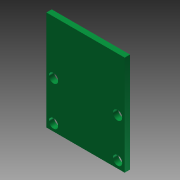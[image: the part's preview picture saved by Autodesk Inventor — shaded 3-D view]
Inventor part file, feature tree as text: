
AUTODESK INVENTOR PART (.ipt)
format: ipt  version: 2014 SP1 (Build 180222100, 222)  size: 98,816 bytes
history: native  units: in
note: dims shown in document units (in); Inventor stores cm internally (conversion verified against a paired STEP export)
features: extrude x2, sketch x1
ambient origin geometry x8: Origin, YZ Plane, XZ Plane, XY Plane, X Axis, Y Axis, Z Axis, Center Point
bodies: Solid1 (feature_tree)
feature tree (3):
  sketch  "Sketch1"  dims[d0=1.1024in d1=0.8661in d2=0.1024in d3=0.7874in d5=0.7087in d6=0.7874in d8=0.4331in d11=0.0787in d12=0.0591in d13=0.0in d14=0.1575in d15=0.1181in d16=0.0394in d17=0.0in]
  extrude  "Extrusion1"  Depth=0.8661in
  extrude  "Extrusion2"  Depth=0.0394in
